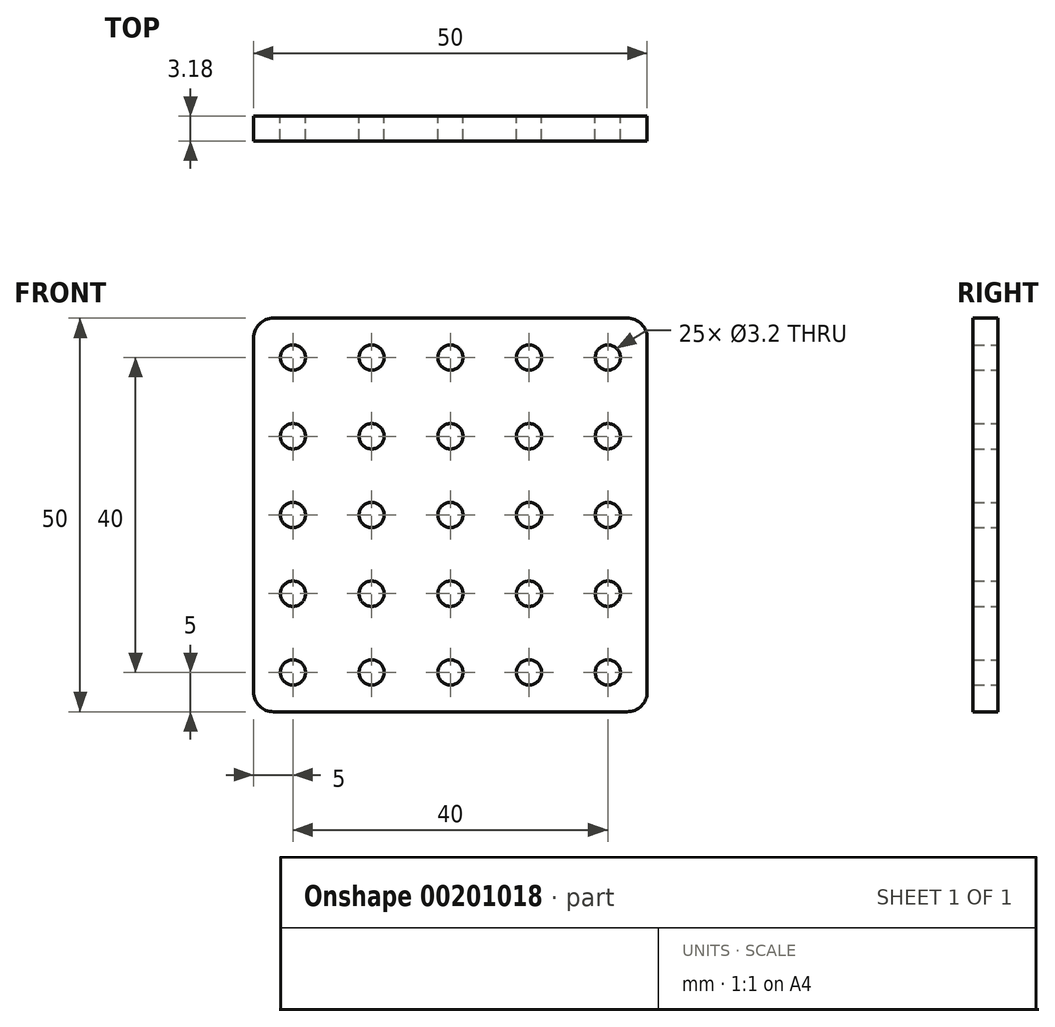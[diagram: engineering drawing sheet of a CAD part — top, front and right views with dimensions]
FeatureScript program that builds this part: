
annotation { "Feature Type Name" : "Feature", "Feature Type Description" : "" }
export const myFeature = defineFeature(function(context is Context, id is Id, definition is map)
    precondition{}
    {
        {
            var Q0;
            Q0=qCreatedBy(makeId("Front.planeOp"),FACE);
            var sketch = newSketch(context, id + "F0", { "sketchPlane" : qUnion([Q0])});
            skLineSegment(sketch, "E0.bottom", {"start": v(2.54, 0) * mm, "end": v(47.46, 0) * mm});
            skLineSegment(sketch, "E0.top", {"start": v(2.54, -50) * mm, "end": v(47.46, -50) * mm});
            skLineSegment(sketch, "E0.left", {"start": v(0, -2.54) * mm, "end": v(0, -47.46) * mm});
            skLineSegment(sketch, "E0.right", {"start": v(50, -2.54) * mm, "end": v(50, -47.46) * mm});
            skPoint(sketch, "E1.visualSharp", {"position": v(0, 0) * mm});
            skArc(sketch, "E1.filletArc", {"start": v(2.54, 0) * mm, "mid": v(0.74, -0.74) * mm, "end": v(0, -2.54) * mm});
            skPoint(sketch, "E2.visualSharp", {"position": v(50, 0) * mm});
            skArc(sketch, "E2.filletArc", {"start": v(50, -2.54) * mm, "mid": v(49.26, -0.74) * mm, "end": v(47.46, 0) * mm});
            skPoint(sketch, "E3.visualSharp", {"position": v(50, -50) * mm});
            skArc(sketch, "E3.filletArc", {"start": v(47.46, -50) * mm, "mid": v(49.26, -49.26) * mm, "end": v(50, -47.46) * mm});
            skPoint(sketch, "E4.visualSharp", {"position": v(0, -50) * mm});
            skArc(sketch, "E4.filletArc", {"start": v(0, -47.46) * mm, "mid": v(0.74, -49.26) * mm, "end": v(2.54, -50) * mm});
            skCircle(sketch, "E5", {"center": v(5, -5) * mm, "radius": 1.6 * mm});
            skCircle(sketch, "E6.0.1.0", {"center": v(5, -15) * mm, "radius": 1.6 * mm});
            skCircle(sketch, "E6.0.2.0", {"center": v(5, -25) * mm, "radius": 1.6 * mm});
            skCircle(sketch, "E6.0.3.0", {"center": v(5, -35) * mm, "radius": 1.6 * mm});
            skCircle(sketch, "E6.0.4.0", {"center": v(5, -45) * mm, "radius": 1.6 * mm});
            skCircle(sketch, "E6.1.0.0", {"center": v(15, -5) * mm, "radius": 1.6 * mm});
            skCircle(sketch, "E6.1.1.0", {"center": v(15, -15) * mm, "radius": 1.6 * mm});
            skCircle(sketch, "E6.1.2.0", {"center": v(15, -25) * mm, "radius": 1.6 * mm});
            skCircle(sketch, "E6.1.3.0", {"center": v(15, -35) * mm, "radius": 1.6 * mm});
            skCircle(sketch, "E6.1.4.0", {"center": v(15, -45) * mm, "radius": 1.6 * mm});
            skCircle(sketch, "E6.2.0.0", {"center": v(25, -5) * mm, "radius": 1.6 * mm});
            skCircle(sketch, "E6.2.1.0", {"center": v(25, -15) * mm, "radius": 1.6 * mm});
            skCircle(sketch, "E6.2.2.0", {"center": v(25, -25) * mm, "radius": 1.6 * mm});
            skCircle(sketch, "E6.2.3.0", {"center": v(25, -35) * mm, "radius": 1.6 * mm});
            skCircle(sketch, "E6.2.4.0", {"center": v(25, -45) * mm, "radius": 1.6 * mm});
            skCircle(sketch, "E6.3.0.0", {"center": v(35, -5) * mm, "radius": 1.6 * mm});
            skCircle(sketch, "E6.3.1.0", {"center": v(35, -15) * mm, "radius": 1.6 * mm});
            skCircle(sketch, "E6.3.2.0", {"center": v(35, -25) * mm, "radius": 1.6 * mm});
            skCircle(sketch, "E6.3.3.0", {"center": v(35, -35) * mm, "radius": 1.6 * mm});
            skCircle(sketch, "E6.3.4.0", {"center": v(35, -45) * mm, "radius": 1.6 * mm});
            skCircle(sketch, "E6.4.0.0", {"center": v(45, -5) * mm, "radius": 1.6 * mm});
            skCircle(sketch, "E6.4.1.0", {"center": v(45, -15) * mm, "radius": 1.6 * mm});
            skCircle(sketch, "E6.4.2.0", {"center": v(45, -25) * mm, "radius": 1.6 * mm});
            skCircle(sketch, "E6.4.3.0", {"center": v(45, -35) * mm, "radius": 1.6 * mm});
            skCircle(sketch, "E6.4.4.0", {"center": v(45, -45) * mm, "radius": 1.6 * mm});
            skLineSegment(sketch, "E6.direction1", {"start": v(5, -5) * mm, "end": v(15, -5) * mm, "construction": true});
            skLineSegment(sketch, "E6.direction2", {"start": v(5, -5) * mm, "end": v(5, -15) * mm, "construction": true});
            skSolve(sketch);
        }
        {
            var Q0;
            Q0=makeQuery(id+"F0.imprint","IMPRINT",FACE,{"disambiguationData":[TD([[makeQuery(id+"F0.imprint","IMPRINT",EDGE,{"derivedFrom":sQuery(id+"F0.wireOp",EDGE,"E0.bottom")}),-1.0]])]});
            extrude(context, id + "F1", {"entities" : qUnion([Q0]), "depth" : 3.17 * mm});
        }
    });
